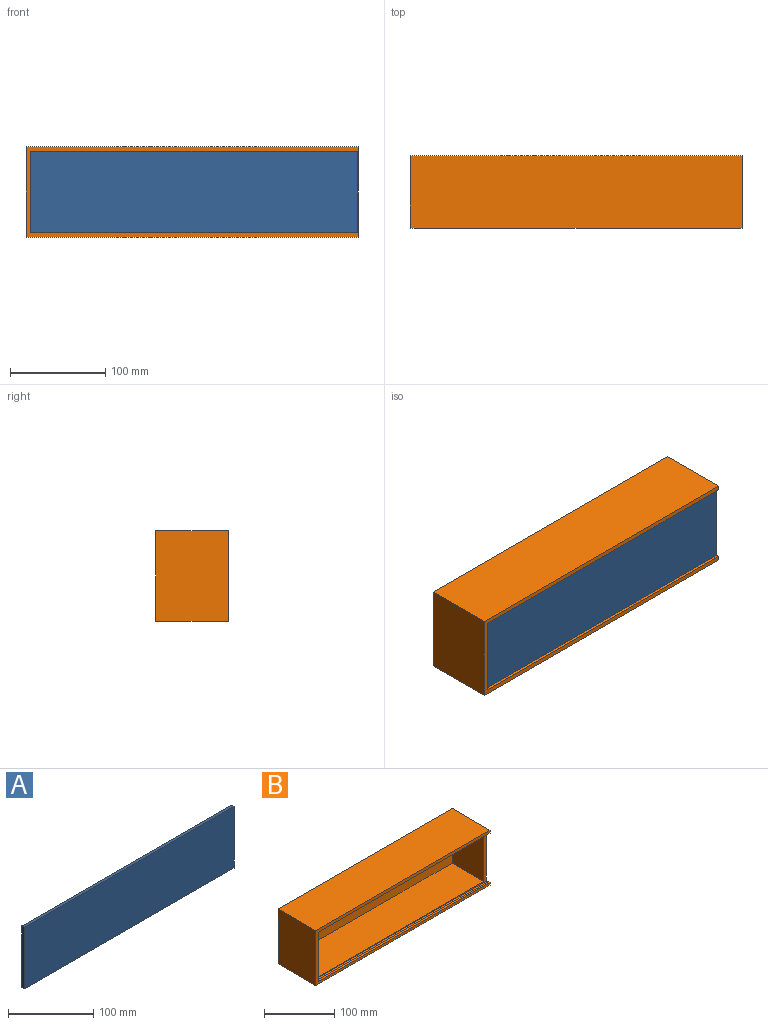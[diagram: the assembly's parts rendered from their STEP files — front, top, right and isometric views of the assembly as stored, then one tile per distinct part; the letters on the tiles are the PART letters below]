
ASSEMBLY  parts=2 mates=1
PART A: 6 faces, bbox 347.5x4.3x88.4 mm
  f0: plane 88.39x4.33mm, normal (-1,0,0), area 382.8mm2, adj f1,f3,f4,f5
  f1: plane 347.47x4.33mm, normal (0,0,-1), area 1505mm2, adj f0,f2,f4,f5
  f2: plane 88.39x4.33mm, normal (1,0,0), area 382.8mm2, adj f1,f3,f4,f5
  f3: plane 347.47x4.33mm, normal (0,0,1), area 1505mm2, adj f0,f2,f4,f5
  f4: plane 347.47x88.39mm, normal (0,1,0), area 30713.7mm2, adj f0,f1,f2,f3
  f5: plane 347.47x88.39mm, normal (0,-1,0), area 30713.7mm2, adj f0,f1,f2,f3
PART B: 23 faces, bbox 349.3x76.2x95.3 mm
  f0: plane 3.18x0.01mm, normal (-1,0,0), area 0mm2, adj f1,f8,f11,f13
  f1: plane 349.25x95.25mm, normal (0,-1,0), area 3735mm2, adj f0,f2,f3,f4,f5,f6,f8,f9
  f2: plane 95.25x76.2mm, normal (1,0,0), area 6561.4mm2, adj f1,f4,f6,f7,f11,f12,f13,f14
  f3: plane 3.18x0.01mm, normal (-1,0,0), area 0mm2, adj f1,f10,f12,f13
  f4: plane 349.25x76.2mm, normal (0,0,1), area 26612.8mm2, adj f1,f2,f5,f7
  f5: plane 95.25x76.2mm, normal (-1,0,0), area 7258.1mm2, adj f1,f4,f6,f7
  f6: plane 349.25x76.2mm, normal (0,0,-1), area 26612.8mm2, adj f1,f2,f5,f7
  f7: plane 349.25x95.25mm, normal (0,1,0), area 33266.1mm2, adj f2,f4,f5,f6
  f8: plane 339.73x3.18mm, normal (0,0,-1), area 1078.6mm2, adj f0,f1,f9,f13
  f9: plane 85.73x3.18mm, normal (1,0,0), area 272.2mm2, adj f1,f8,f10,f13
  f10: plane 339.73x3.18mm, normal (0,0,1), area 1078.6mm2, adj f1,f3,f9,f13
  f11: plane 4.76x3.18mm, normal (0,0,-1), area 15.1mm2, adj f0,f1,f2,f13
  f12: plane 4.76x3.18mm, normal (0,0,1), area 15.1mm2, adj f1,f2,f3,f13
  f13: plane 347.66x88.9mm, normal (0,1,0), area 1376.1mm2, adj f0,f2,f3,f8,f9,f10,f11,f12
  f14: plane 347.66x88.9mm, normal (0,-1,0), area 1784.3mm2, adj f2,f15,f16,f17,f19,f20,f21,f22
  f15: plane 88.9x4.78mm, normal (1,0,0), area 424.5mm2, adj f13,f14,f16,f17
  f16: plane 347.66x4.78mm, normal (0,0,1), area 1660.2mm2, adj f2,f13,f14,f15
  f17: plane 347.66x4.78mm, normal (0,0,-1), area 1660.2mm2, adj f2,f13,f14,f15
  f18: plane 339.73x85.73mm, normal (0,-1,0), area 29122.9mm2, adj f19,f20,f21,f22
  f19: plane 339.73x63.49mm, normal (0,0,1), area 21568.2mm2, adj f14,f18,f20,f22
  f20: plane 85.73x63.49mm, normal (1,0,0), area 5442.4mm2, adj f14,f18,f19,f21
  f21: plane 339.73x63.49mm, normal (0,0,-1), area 21568.2mm2, adj f14,f18,f20,f22
  f22: plane 85.73x63.49mm, normal (-1,0,0), area 5442.4mm2, adj f14,f18,f19,f21
PLACE A t=(17.69,-31.31,-136.16)mm
PLACE B t=(16.99,37.16,1.15)mm fixed
MATE slider B.f15 <-> A.f0  axis (-1,0,0) through (-156.05,-33.48,1.15)mm
